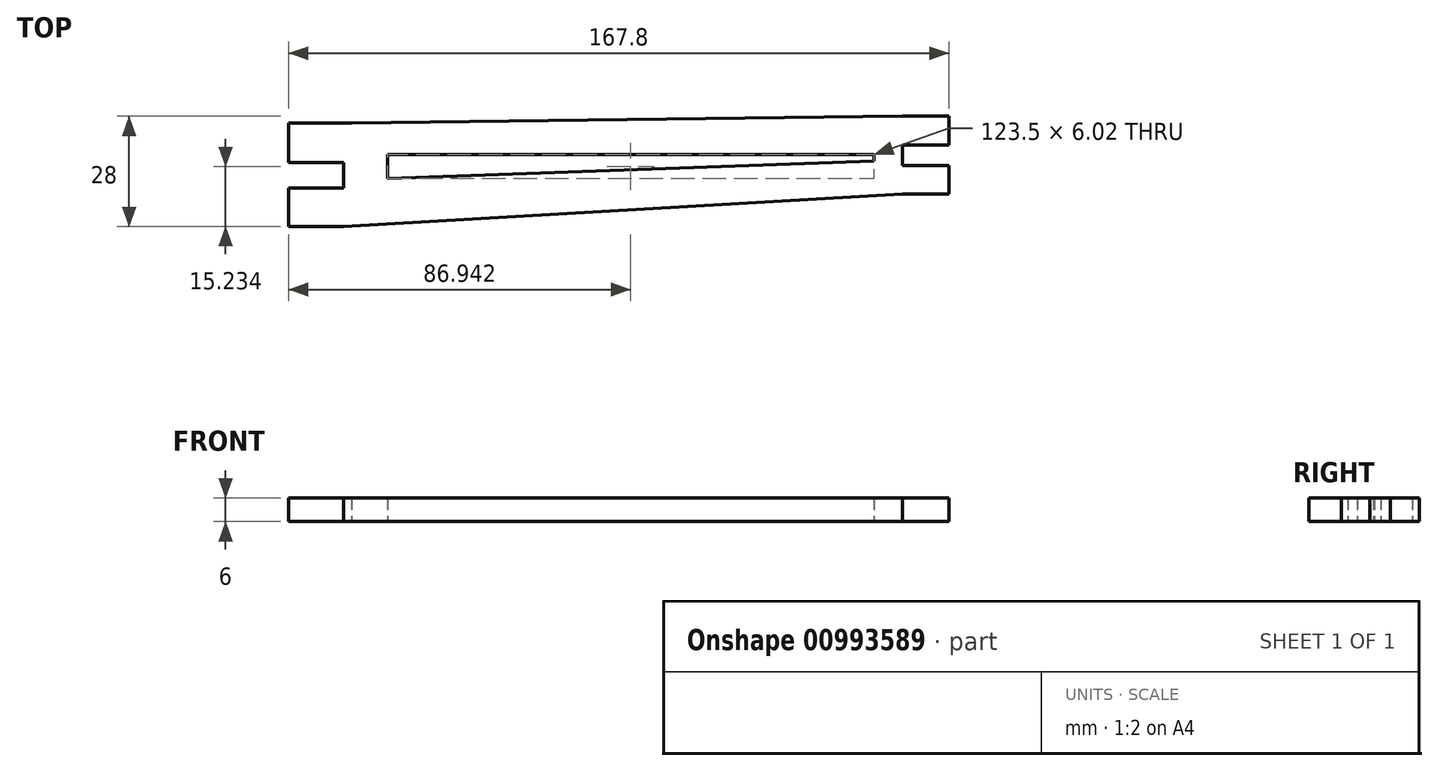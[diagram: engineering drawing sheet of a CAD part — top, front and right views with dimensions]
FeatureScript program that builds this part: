
annotation { "Feature Type Name" : "Feature", "Feature Type Description" : "" }
export const myFeature = defineFeature(function(context is Context, id is Id, definition is map)
    precondition{}
    {
        {
            var Q0;
            Q0=qCreatedBy(makeId("Top.planeOp"),FACE);
            var sketch = newSketch(context, id + "F0", { "sketchPlane" : qUnion([Q0])});
            skLineSegment(sketch, "E0.bottom", {"start": v(46.15, 35.29) * mm, "end": v(51.95, 35.29) * mm});
            skLineSegment(sketch, "E0.top", {"start": v(46.15, 27.99) * mm, "end": v(51.95, 27.99) * mm});
            skLineSegment(sketch, "E0.left", {"start": v(46.15, 35.29) * mm, "end": v(46.15, 27.99) * mm});
            skLineSegment(sketch, "E0.right", {"start": v(51.95, 35.29) * mm, "end": v(51.95, 27.99) * mm});
            skLineSegment(sketch, "E1.bottom", {"start": v(46.15, 22.79) * mm, "end": v(51.95, 22.79) * mm});
            skLineSegment(sketch, "E1.top", {"start": v(46.15, 15.49) * mm, "end": v(51.95, 15.49) * mm});
            skLineSegment(sketch, "E1.left", {"start": v(46.15, 22.79) * mm, "end": v(46.15, 15.49) * mm});
            skLineSegment(sketch, "E1.right", {"start": v(51.95, 22.79) * mm, "end": v(51.95, 15.49) * mm});
            skLineSegment(sketch, "E2.bottom", {"start": v(46.15, 35.29) * mm, "end": v(40.15, 35.29) * mm});
            skLineSegment(sketch, "E2.top", {"start": v(46.15, 27.99) * mm, "end": v(40.15, 27.99) * mm});
            skLineSegment(sketch, "E2.right", {"start": v(40.15, 35.29) * mm, "end": v(40.15, 27.99) * mm});
            skLineSegment(sketch, "E3.bottom", {"start": v(46.15, 22.79) * mm, "end": v(46.15, 22.79) * mm});
            skLineSegment(sketch, "E3.top", {"start": v(46.15, 15.49) * mm, "end": v(46.15, 15.49) * mm});
            skLineSegment(sketch, "E4.bottom", {"start": v(40.15, 22.79) * mm, "end": v(46.15, 22.79) * mm});
            skLineSegment(sketch, "E4.top", {"start": v(40.15, 15.49) * mm, "end": v(46.15, 15.49) * mm});
            skLineSegment(sketch, "E4.left", {"start": v(40.15, 22.79) * mm, "end": v(40.15, 15.49) * mm});
            skLineSegment(sketch, "E5.bottom", {"start": v(40.15, 35.29) * mm, "end": v(-99.85, 33.59) * mm});
            skLineSegment(sketch, "E5.left", {"start": v(40.15, 35.29) * mm, "end": v(40.15, 15.49) * mm});
            skLineSegment(sketch, "E6.bottom", {"start": v(-90.66, 25.53) * mm, "end": v(32.84, 25.53) * mm});
            skLineSegment(sketch, "E6.left", {"start": v(-90.66, 25.53) * mm, "end": v(-90.66, 19.52) * mm});
            skLineSegment(sketch, "E6.right", {"start": v(32.84, 25.53) * mm, "end": v(32.84, 23.9) * mm});
            skLineSegment(sketch, "E7", {"start": v(-101.85, 7.29) * mm, "end": v(40.15, 15.49) * mm});
            skLineSegment(sketch, "E8.left", {"start": v(-90.66, 19.52) * mm, "end": v(-90.66, 19.52) * mm});
            skLineSegment(sketch, "E9", {"start": v(-90.66, 19.52) * mm, "end": v(32.84, 23.9) * mm});
            skLineSegment(sketch, "E10.bottom", {"start": v(-99.85, 33.59) * mm, "end": v(-115.85, 33.59) * mm});
            skLineSegment(sketch, "E11.bottom", {"start": v(-115.85, 23.59) * mm, "end": v(-101.85, 23.59) * mm});
            skLineSegment(sketch, "E11.right", {"start": v(-101.85, 23.59) * mm, "end": v(-101.85, 17.09) * mm});
            skLineSegment(sketch, "E12", {"start": v(-115.85, 33.59) * mm, "end": v(-115.85, 23.59) * mm});
            skLineSegment(sketch, "E13.bottom", {"start": v(-101.85, 17.09) * mm, "end": v(-115.85, 17.09) * mm});
            skLineSegment(sketch, "E13.top", {"start": v(-101.85, 7.29) * mm, "end": v(-115.85, 7.29) * mm});
            skLineSegment(sketch, "E13.right", {"start": v(-115.85, 17.09) * mm, "end": v(-115.85, 7.29) * mm});
            skLineSegment(sketch, "E14.bottom", {"start": v(-101.85, 23.59) * mm, "end": v(-109.85, 23.59) * mm});
            skSolve(sketch);
        }
        {
            var Q0;
            {var subQ0=makeQuery(id+"F0.imprint","IMPRINT",EDGE,{"derivedFrom":sQuery(id+"F0.wireOp",EDGE,"E2.right")});var subQ6=makeQuery(id+"F0.imprint","IMPRINT",EDGE,{"derivedFrom":sQuery(id+"F0.wireOp",EDGE,"E1.left")});var subQ7=makeQuery(id+"F0.imprint","IMPRINT",EDGE,{"derivedFrom":sQuery(id+"F0.wireOp",EDGE,"E0.left")});Q0=qUnion([makeQuery(id+"F0.imprint","IMPRINT",FACE,{"disambiguationData":[TD([[makeQuery(id+"F0.imprint","IMPRINT",EDGE,{"derivedFrom":sQuery(id+"F0.wireOp",EDGE,"E0.bottom")}),-1.0]])]}),makeQuery(id+"F0.imprint","IMPRINT",FACE,{"disambiguationData":[TD([[makeQuery(id+"F0.imprint","IMPRINT",EDGE,{"derivedFrom":sQuery(id+"F0.wireOp",EDGE,"E1.bottom")}),-1.0]])]}),makeQuery(id+"F0.imprint","IMPRINT",FACE,{"disambiguationData":[TD([[subQ7,-1.0]])]}),makeQuery(id+"F0.imprint","IMPRINT",FACE,{"disambiguationData":[TD([[subQ6,-1.0]])]}),makeQuery(id+"F0.imprint","IMPRINT",FACE,{"disambiguationData":[TD([[subQ0,-1.0]])]})]);}
            extrude(context, id + "F1", {"entities" : qUnion([Q0]), "depth" : 6 * mm, "offsetDistance" : 25 * mm});
        }
    });
